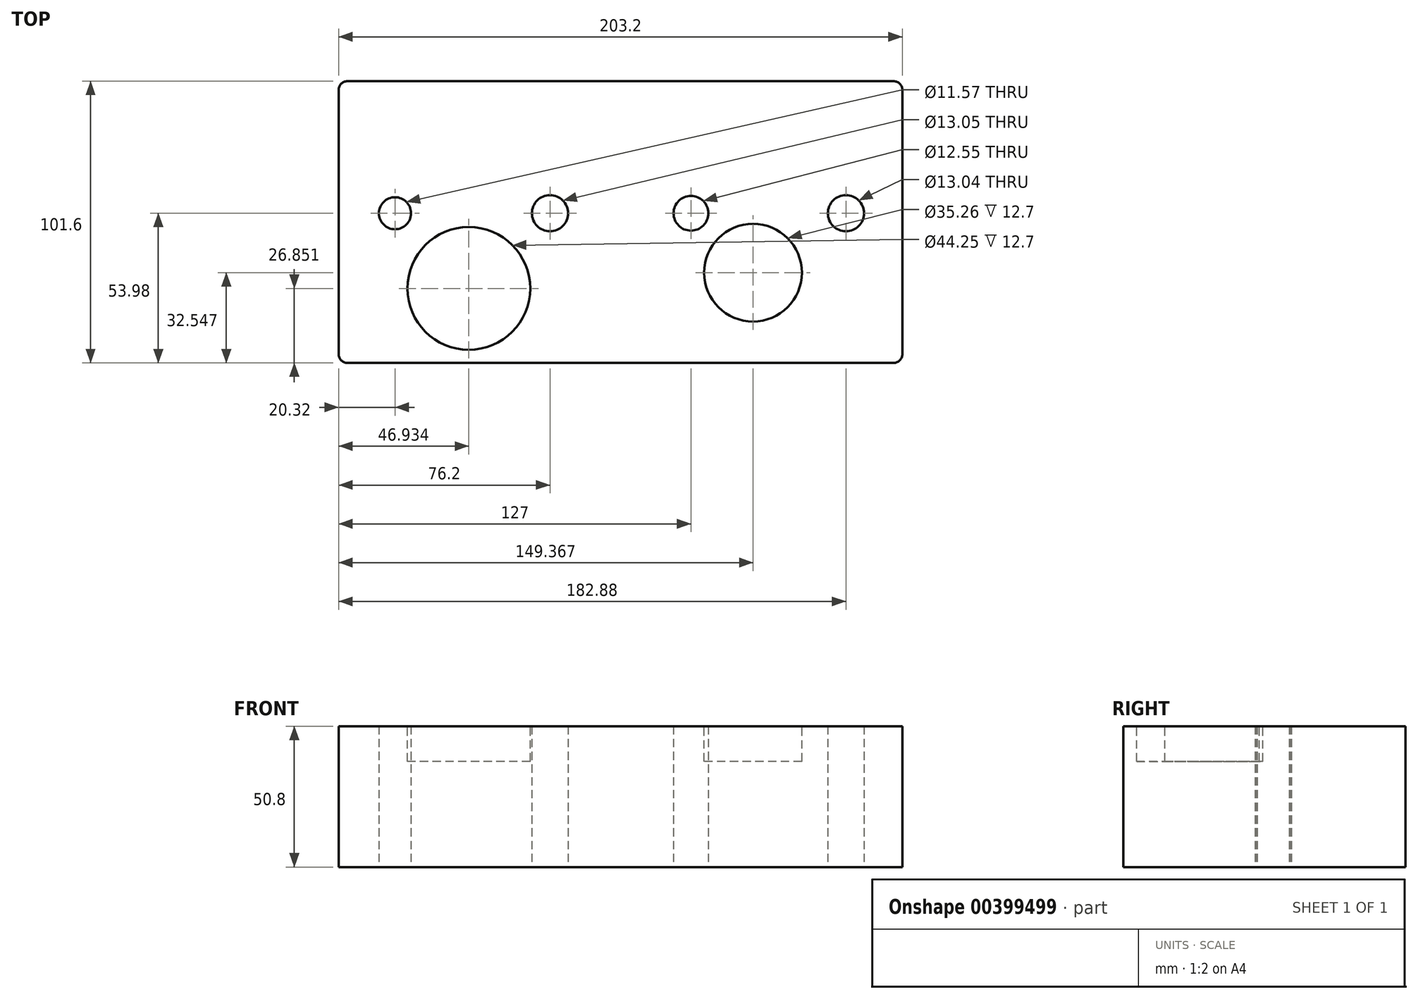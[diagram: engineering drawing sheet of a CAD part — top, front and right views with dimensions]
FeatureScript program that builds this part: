
annotation { "Feature Type Name" : "Feature", "Feature Type Description" : "" }
export const myFeature = defineFeature(function(context is Context, id is Id, definition is map)
    precondition{}
    {
        {
            var Q0;
            Q0=qCreatedBy(makeId("Top.planeOp"),FACE);
            var sketch = newSketch(context, id + "F0", { "sketchPlane" : qUnion([Q0])});
            skLineSegment(sketch, "E0.bottom", {"start": v(-98.42, -53.98) * mm, "end": v(98.43, -53.97) * mm});
            skLineSegment(sketch, "E0.top", {"start": v(-98.42, 47.62) * mm, "end": v(98.43, 47.63) * mm});
            skLineSegment(sketch, "E0.left", {"start": v(-101.6, -50.8) * mm, "end": v(-101.6, 44.45) * mm});
            skLineSegment(sketch, "E0.right", {"start": v(101.6, -50.8) * mm, "end": v(101.6, 44.45) * mm});
            skPoint(sketch, "E0.middle", {"position": v(0, 0) * mm});
            skPoint(sketch, "E1.visualSharp", {"position": v(-101.6, 47.62) * mm});
            skArc(sketch, "E1.filletArc", {"start": v(-98.42, 47.62) * mm, "mid": v(-100.67, 46.7) * mm, "end": v(-101.6, 44.45) * mm});
            skPoint(sketch, "E2.newPointB", {"position": v(-101.6, -53.98) * mm});
            skArc(sketch, "E2.filletArc", {"start": v(-101.6, -50.8) * mm, "mid": v(-100.67, -53.05) * mm, "end": v(-98.42, -53.98) * mm});
            skPoint(sketch, "E3.newPointB", {"position": v(101.6, -53.97) * mm});
            skArc(sketch, "E3.filletArc", {"start": v(98.43, -53.97) * mm, "mid": v(100.67, -53.05) * mm, "end": v(101.6, -50.8) * mm});
            skArc(sketch, "E4.filletArc", {"start": v(101.6, 44.45) * mm, "mid": v(100.67, 46.7) * mm, "end": v(98.43, 47.63) * mm});
            skLineSegment(sketch, "E5", {"start": v(-25.4, 11.47) * mm, "end": v(-25.4, -34.82) * mm, "construction": true});
            skLineSegment(sketch, "E6", {"start": v(-81.28, 8.6) * mm, "end": v(-81.28, -31.65) * mm, "construction": true});
            skLineSegment(sketch, "E7", {"start": v(25.4, 11.47) * mm, "end": v(25.4, -34.82) * mm, "construction": true});
            skLineSegment(sketch, "E8", {"start": v(81.28, 13.49) * mm, "end": v(81.28, -34.82) * mm, "construction": true});
            skLineSegment(sketch, "E9", {"start": v(-109.83, 0) * mm, "end": v(121.05, 0) * mm, "construction": true});
            skCircle(sketch, "E10", {"center": v(-81.28, 0) * mm, "radius": 5.79 * mm});
            skCircle(sketch, "E11", {"center": v(-25.4, 0) * mm, "radius": 6.52 * mm});
            skCircle(sketch, "E12", {"center": v(25.4, 0) * mm, "radius": 6.28 * mm});
            skCircle(sketch, "E13", {"center": v(81.28, 0) * mm, "radius": 6.52 * mm});
            skSolve(sketch);
        }
        {
            var Q0;
            Q0 = qSketchRegion(id + "F0", true);
            extrude(context, id + "F1", {"entities" : qUnion([Q0]), "depth" : 50.8 * mm});
        }
        {
            var Q0;
            Q0=makeQuery(id+"F1.opExtrude","CAP_FACE",FACE,{"disambiguationData":[OSD([sQuery(id+"F0.wireOp",EDGE,"E0.bottom"),sQuery(id+"F0.wireOp",EDGE,"E0.top"),sQuery(id+"F0.wireOp",EDGE,"E0.left"),sQuery(id+"F0.wireOp",EDGE,"E0.right"),sQuery(id+"F0.wireOp",EDGE,"E1.filletArc"),sQuery(id+"F0.wireOp",EDGE,"E2.filletArc"),sQuery(id+"F0.wireOp",EDGE,"E3.filletArc"),sQuery(id+"F0.wireOp",EDGE,"E4.filletArc"),sQuery(id+"F0.wireOp",EDGE,"E10"),sQuery(id+"F0.wireOp",EDGE,"E11"),sQuery(id+"F0.wireOp",EDGE,"E12"),sQuery(id+"F0.wireOp",EDGE,"E13")])],"isStart":false});
            var sketch = newSketch(context, id + "F2", { "sketchPlane" : qUnion([Q0])});
            skCircle(sketch, "E14", {"center": v(-54.67, -27.13) * mm, "radius": 22.12 * mm});
            skCircle(sketch, "E15", {"center": v(47.77, -21.43) * mm, "radius": 17.63 * mm});
            skSolve(sketch);
        }
        {
            var Q0;
            Q0 = qSketchRegion(id + "F2", true);
            extrude(context, id + "F3", {"entities" : qUnion([Q0]), "operationType" : NewBodyOperationType.REMOVE, "oppositeDirection" : true, "depth" : 12.7 * mm});
        }
    });
